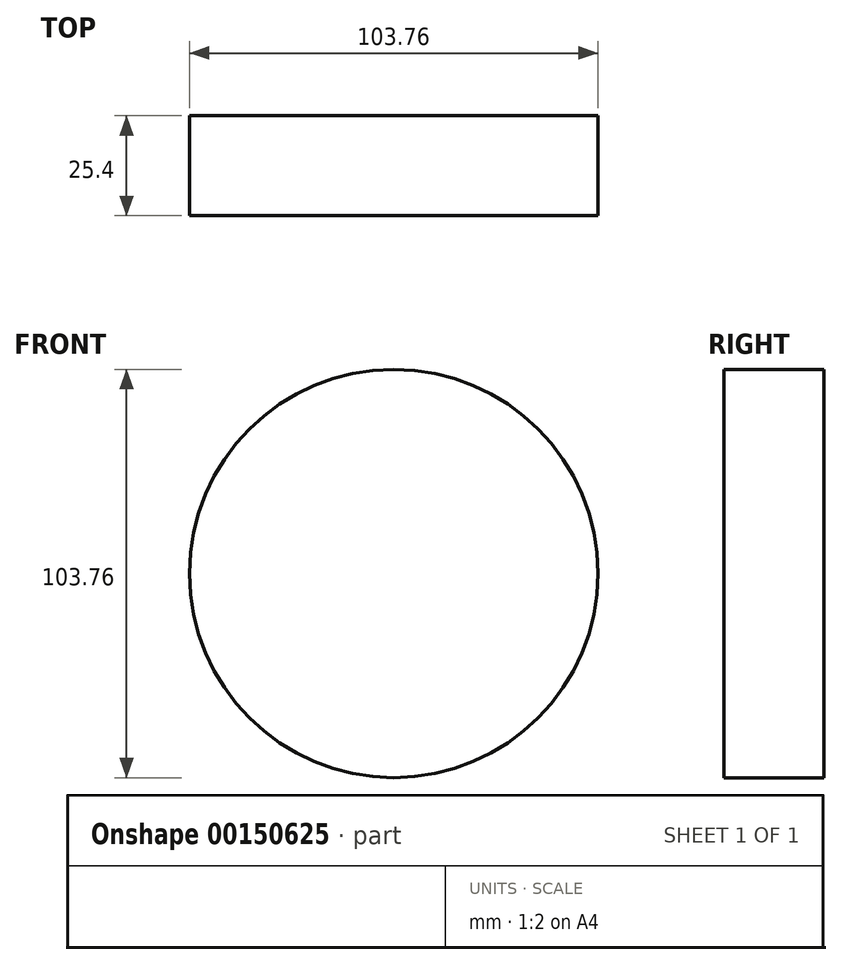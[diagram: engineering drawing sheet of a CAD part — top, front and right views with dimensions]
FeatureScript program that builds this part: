
annotation { "Feature Type Name" : "Feature", "Feature Type Description" : "" }
export const myFeature = defineFeature(function(context is Context, id is Id, definition is map)
    precondition{}
    {
        {
            var Q0;
            Q0=qCreatedBy(makeId("Front.planeOp"),FACE);
            var sketch = newSketch(context, id + "F0", { "sketchPlane" : qUnion([Q0])});
            skCircle(sketch, "E0", {"center": v(0, 0) * mm, "radius": 51.88 * mm});
            skSolve(sketch);
        }
        {
            var Q0;
            Q0 = qSketchRegion(id + "F0", true);
            extrude(context, id + "F1", {"entities" : qUnion([Q0]), "depth" : 25.4 * mm});
        }
    });
